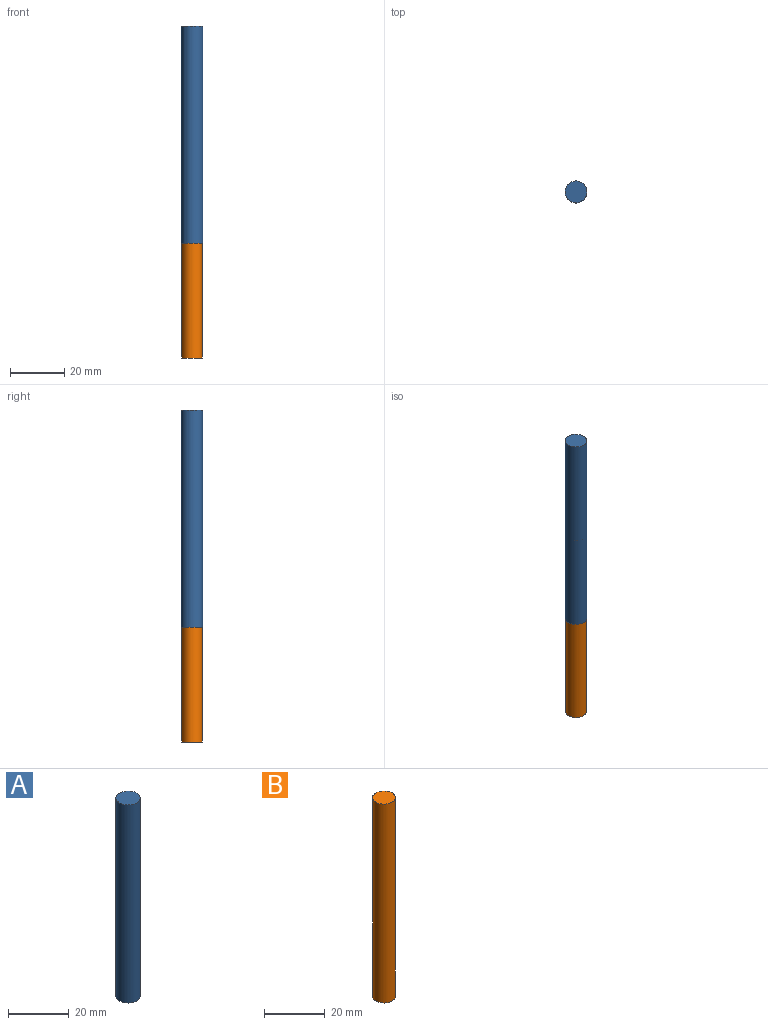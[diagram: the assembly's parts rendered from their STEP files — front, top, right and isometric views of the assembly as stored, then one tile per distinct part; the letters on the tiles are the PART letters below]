
ASSEMBLY  parts=2 mates=1
PART A: 3 faces, bbox 8x8x80 mm
  f0: cylinder r=4mm len=80mm, axis (0,0,-1), area 2010.6mm2, adj f1,f2
  f1: plane 8x8mm, normal (0,0,1), area 50.3mm2, adj f0
  f2: plane 8x8mm, normal (0,0,-1), area 50.3mm2, adj f0
PART B: 3 faces, bbox 7.5x7.5x80 mm
  f0: cylinder r=3.75mm len=80mm, axis (0,0,-1), area 1885mm2, adj f1,f2
  f1: plane 7.5x7.5mm, normal (0,0,1), area 44.2mm2, adj f0
  f2: plane 7.5x7.5mm, normal (0,0,-1), area 44.2mm2, adj f0
PLACE A t=(-45,-3.48,25.26)mm
PLACE B t=(-45,-3.48,-96.94)mm
MATE slider B.f0 <-> A.f0  axis (0,0,1) through (-45,-3.48,63.06)mm
